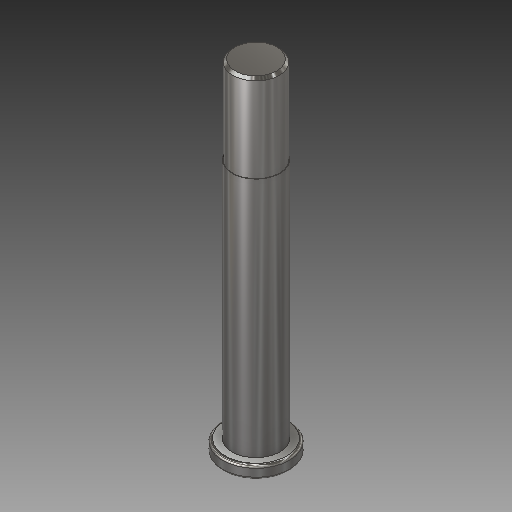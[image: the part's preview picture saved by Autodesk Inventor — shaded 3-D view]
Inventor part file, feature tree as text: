
AUTODESK INVENTOR PART (.ipt)
format: ipt  version: 2019.3 (Build 233278000, 278)  size: 125,952 bytes
history: native  units: mm
features: other x1, revolve x1, fillet x1, chamfer x1, sketch x1
ambient origin geometry x8: Origin, YZ Plane, XZ Plane, XY Plane, X Axis, Y Axis, Z Axis, Center Point
bodies: Body1 (feature_tree)
feature tree (5):
  other  "Твердое тело1"
  revolve  "Вращение1"
  fillet  "Сопряжение1"  Radius=64.0mm
  chamfer  "Фаска1"  Distance=9.3mm
  sketch  "Эскиз1"
